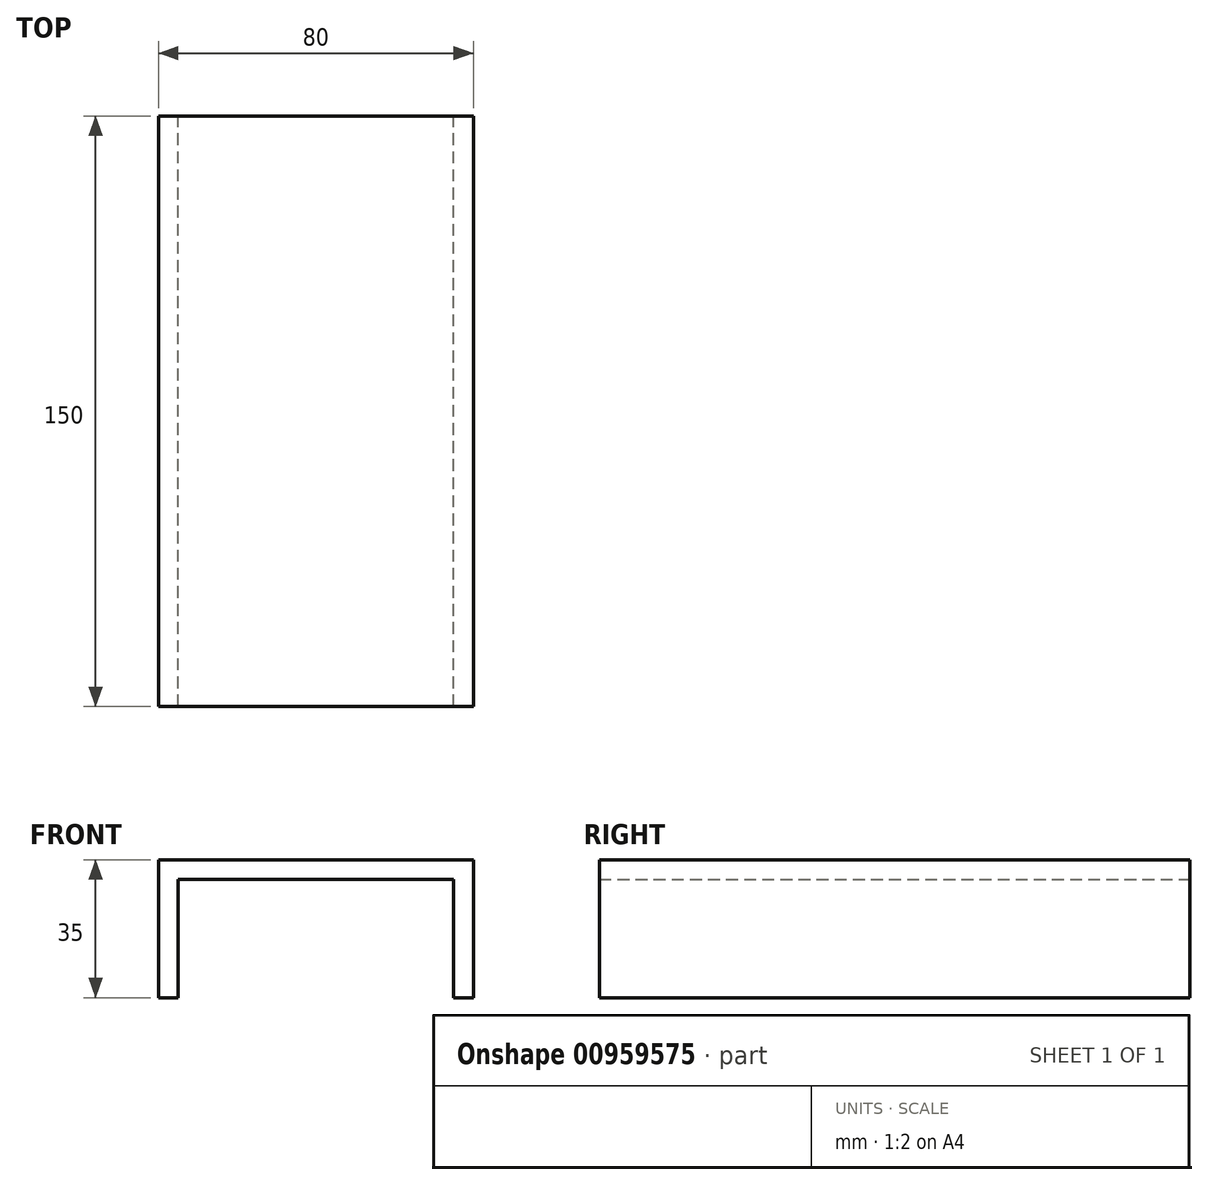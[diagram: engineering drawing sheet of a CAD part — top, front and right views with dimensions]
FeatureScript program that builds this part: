
annotation { "Feature Type Name" : "Feature", "Feature Type Description" : "" }
export const myFeature = defineFeature(function(context is Context, id is Id, definition is map)
    precondition{}
    {
        {
            var Q0;
            Q0=qCreatedBy(makeId("Front.planeOp"),FACE);
            var sketch = newSketch(context, id + "F0", { "sketchPlane" : qUnion([Q0])});
            skLineSegment(sketch, "E0", {"start": v(-55.66, 37.12) * mm, "end": v(-55.66, 7.12) * mm});
            skLineSegment(sketch, "E1", {"start": v(-55.66, 37.12) * mm, "end": v(14.34, 37.12) * mm});
            skLineSegment(sketch, "E2", {"start": v(14.34, 37.12) * mm, "end": v(14.34, 7.12) * mm});
            skLineSegment(sketch, "E3", {"start": v(-55.66, 7.12) * mm, "end": v(-60.66, 7.12) * mm});
            skLineSegment(sketch, "E4", {"start": v(-60.66, 7.12) * mm, "end": v(-60.66, 42.12) * mm});
            skLineSegment(sketch, "E5", {"start": v(14.34, 7.12) * mm, "end": v(19.34, 7.12) * mm});
            skLineSegment(sketch, "E6", {"start": v(19.34, 7.12) * mm, "end": v(19.34, 42.12) * mm});
            skLineSegment(sketch, "E7", {"start": v(-60.66, 42.12) * mm, "end": v(19.34, 42.12) * mm});
            skSolve(sketch);
        }
        {
            var Q0;
            Q0=makeQuery(id+"F0.imprint","IMPRINT",FACE,{"disambiguationData":[TD([[makeQuery(id+"F0.imprint","IMPRINT",EDGE,{"derivedFrom":sQuery(id+"F0.wireOp",EDGE,"E0")}),-1.0]])]});
            extrude(context, id + "F1", {"entities" : qUnion([Q0]), "depth" : 150 * mm, "offsetDistance" : 25 * mm});
        }
    });
